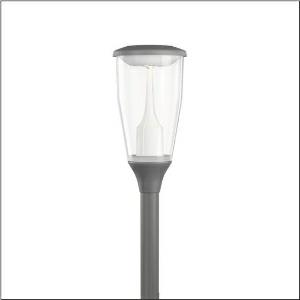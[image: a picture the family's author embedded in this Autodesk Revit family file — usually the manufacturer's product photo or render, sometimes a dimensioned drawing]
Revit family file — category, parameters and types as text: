
# Revit family: dl_11_iq___p1_0a_5xa5565lf14h000022_286d
name_source: partatom
category: Lighting Fixtures
units: mm (PartAtom-declared; Revit-internal decimal feet)

## family parameters
Cut with Voids When Loaded = No
Host = Face
Light Source = No
Part Type = Normal
Room Calculation Point = No
Round Connector Dimension = Use Diameter
Shared = No

## types (1)
- --- (1 x LED, 1530 lm, 10 W, 4000K)
    Apparent Load = 10 VA
    CIE Flux Codes = 34 63 91 95 100
    Color Rendering = 70
    Color Temperature = 4000K
    Default Elevation = 1800 mm
    Description = DL 11 iQ, mast luminaire, Module 540 iQ-SR, primary light control with 3 zone facetted reflector, of plastic, silver coated, highly specular, structured, primary optical cover: cover, of PMMA, transparent, light distribution: P1.0a, light emission: direct distribution, primary light characteristic: asymmetric, installation type: post-top, LED, High Power LED, rated luminous flux: 1.560lm, luminous efficacy: 149lm/W, light colour: 740, colour temperature: 4000K, control gear: iQ Street-Remote, control: Street-Remote, Auto-Match, Temp-Guard, Lumen-Switch, Night-Set, Smart-Wire, Light-Fading, Desk-Remote (wireless, voltage-free reading and setting of iQ features in the workshop via application-optimized NFC function/RFID function), optimised constant luminous flux control (CLO 2.0), mains connection: 220..240V, AC, 50/60Hz, connection cable pre-assembled, cable length: 5,5m, start of lifetime: 10W, end of service life: 10W, reduction: 5W, luminaire housing, upper part, of diecast aluminium, coated, SITECO metallic grey (DB 702S), spigot size: 60mm (post-top), mounting height: 3..5m, post-top mast mounting element, of diecast aluminium, coated, SITECO metallic grey (DB 702S), Module 540 iQ-SR, traffic white (RAL 9016), equipment: standard, protection rating (complete): IP66, insulation class (complete): insulation class II (safety insulation), certification: CE, ENEC, ENEC+, VDE, impact resistance: IK07, packaging unit: 1 piece

Light Distribution: P1.0a
    Height = 665 mm
    Lamp = 1 x LED
    Lamp Light Flux = 1530 lm
    Lamp Power = 10 W
    Lamp count = 1
    Length = 334 mm
    Luminous efficacy = 153 lm/W
    Manufacturer = Siteco
    ModVariant = No
    Model = 5XA5565LF14H000022
    Number of Poles = 1
    OnlyDefault = Yes
    Power Factor = 1
    Product Name = DL 11 iQ | P1.0a
    Product group = mast luminaire | pylon top
    ProductGroupID = 6100
    Protection Class = Protection class II
    Protection Degree = IP 66
    RLX_Detail_Level = 1
    RLX_Emergency_Light_Flux = 0 lm
    RLX_Emergency_Type = 0
    RLX_Emergency_Type_DB = No
    RlxData = <blob elided: 107645 chars, md5=ebd2f25a>
    Socket = socket
    Standby Power = 0 W
    System Light Flux = 1530 lm
    System Power = 10 W
    Type Comments = factory setting: luminous flux: 100 % | dim-lin: 254 | 401 mA
    Type Image = l_1258354.jpg
    URL = http://relux.com
    VarID = @adj_095713
    Voltage = 0 V
    Weight = 0.00 kg
    Width = 0 mm  [stored 0 ft]

note: [stored X ft] marks values corroborated as IEEE doubles in the binary element streams (Revit-internal decimal feet)

## geometry (parser evidence)
native form markers: Blend x4, Sweep x11
no freeform markers — native parametric forms only
